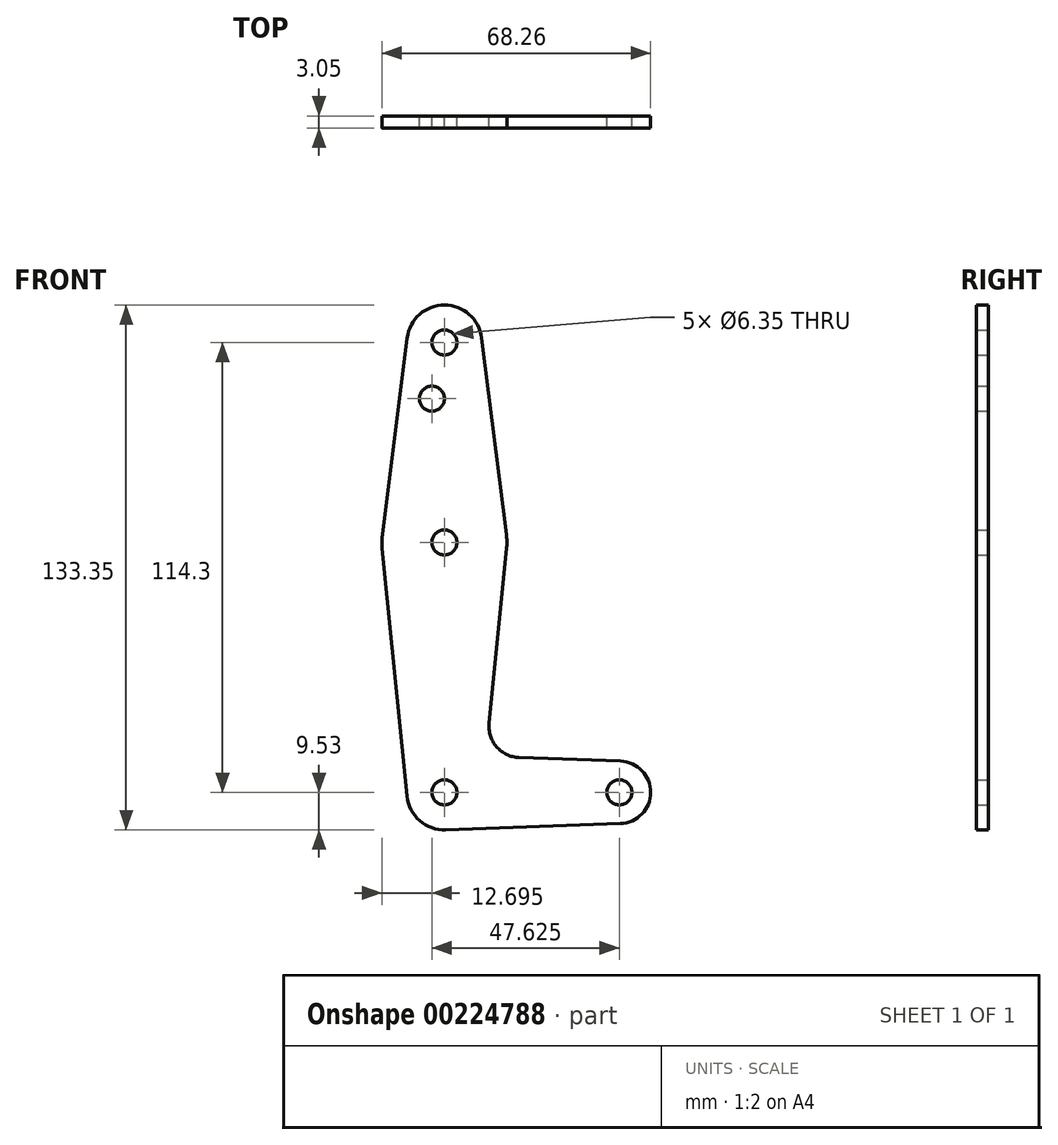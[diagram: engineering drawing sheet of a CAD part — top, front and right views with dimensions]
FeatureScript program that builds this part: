
annotation { "Feature Type Name" : "Feature", "Feature Type Description" : "" }
export const myFeature = defineFeature(function(context is Context, id is Id, definition is map)
    precondition{}
    {
        {
            var Q0;
            Q0=qCreatedBy(makeId("Front.planeOp"),FACE);
            var sketch = newSketch(context, id + "F0", { "sketchPlane" : qUnion([Q0])});
            skCircle(sketch, "E0", {"center": v(0, 0) * mm, "radius": 15.88 * mm});
            skCircle(sketch, "E1", {"center": v(0, 50.8) * mm, "radius": 9.53 * mm});
            skLineSegment(sketch, "E2", {"start": v(0, 50.8) * mm, "end": v(0, -63.5) * mm, "construction": true});
            skLineSegment(sketch, "E3", {"start": v(0, -63.5) * mm, "end": v(44.45, -63.5) * mm, "construction": true});
            skCircle(sketch, "E4", {"center": v(0, -63.5) * mm, "radius": 9.53 * mm});
            skCircle(sketch, "E5", {"center": v(44.45, -63.5) * mm, "radius": 7.94 * mm});
            skLineSegment(sketch, "E6", {"start": v(-9.45, 52) * mm, "end": v(-15.75, 1.98) * mm});
            skLineSegment(sketch, "E7", {"start": v(-9.48, -64.45) * mm, "end": v(-15.8, -1.59) * mm});
            skLineSegment(sketch, "E8", {"start": v(9.45, 52) * mm, "end": v(15.75, 1.98) * mm});
            skLineSegment(sketch, "E9", {"start": v(11.34, -45.9) * mm, "end": v(15.8, -1.59) * mm});
            skCircle(sketch, "E10", {"center": v(0, 50.8) * mm, "radius": 3.18 * mm});
            skCircle(sketch, "E11", {"center": v(0, 0) * mm, "radius": 3.18 * mm});
            skCircle(sketch, "E12", {"center": v(0, -63.5) * mm, "radius": 3.18 * mm});
            skCircle(sketch, "E13", {"center": v(44.45, -63.5) * mm, "radius": 3.18 * mm});
            skCircle(sketch, "E14", {"center": v(-3.17, 36.53) * mm, "radius": 3.18 * mm});
            skLineSegment(sketch, "E15", {"start": v(18.97, -54.65) * mm, "end": v(44.73, -55.57) * mm});
            skLineSegment(sketch, "E16", {"start": v(0.34, -73.02) * mm, "end": v(44.73, -71.43) * mm});
            skPoint(sketch, "E17.newPointB", {"position": v(9.48, -64.45) * mm});
            skArc(sketch, "E17.filletArc", {"start": v(11.34, -45.9) * mm, "mid": v(13.26, -51.93) * mm, "end": v(18.97, -54.65) * mm});
            skSolve(sketch);
        }
        {
            var Q0;
            Q0 = qSketchRegion(id + "F0", true);
            extrude(context, id + "F1", {"entities" : qUnion([Q0]), "depth" : 3.05 * mm});
        }
    });
